# Revit family: 3034797 Sylvania Lighting Fixture GIOTTO335 LED G2 3000K SURFACE
name_source: partatom
category: Lighting Fixtures
revit_build: Autodesk Revit 2016 (Build: 20150220_1215(x64)
units: mm (PartAtom-declared; Revit-internal decimal feet)

## family parameters
Cut with Voids When Loaded = No
Host = Face
Light Source = Yes
OmniClass Number = 23.80.70.00
OmniClass Title = Lighting
Part Type = Normal
Room Calculation Point = No
Round Connector Dimension = Use Diameter
Shared = No

## types (1)
- 3034797 GIOTTO335 LED G2 SURFACE 3000K
    Apparent Load = 23 VA
    Assembly Code = D5020200
    AssetType = Fixed
    ClassificationName = Uniclass2015
    ClassificationValue = EF_70_80
    Color Filter = 16777215
    Cost = 0 $
    Default Elevation = 1219 mm
    Description = Ambient and decorative round, surface mounted LED bulkhead luminaire. White robust polycarbonate body with opal diffuser, 2111 lm, 23W, 92lm/W, 3000K, CRI 80, non-dimmable, 50,000 hours lumen maintenance. Drive current: 700mA, IP44, IK10, Class I, 220-240V, Energy class: A++, A+, A.
    Diameter_SYL = 335 mm  [stored 1.09908 ft]
    DiffuserRadius_SYL = 283 mm
    Dimming Lamp Color Temperature Shift = <None>
    DocumentationLiterature = http://www.sylvania-lighting.com
    DurationUnit = hours
    ElectricShockClassification = Class I
    Emit Shape Visible in Rendering = No
    Emit from Circle Diameter = 317 mm  [stored 1.04003 ft]
    ExpectedLife = 50000
    Height_SYL = 110 mm  [stored 0.360892 ft]
    IfcExportAs = IfcLightFixtureType
    IfcExportType = IfcLightFixtureType
    ImpactProtectionIndex = IK10
    IngressProtection = IP44
    Keynote = 16500
    Lamp = LED
    LampColourRenderingIndex = 80
    LampColourTemperature = 3000 K
    LampNominalLuminous = 2111 lm
    LampsType = LED
    LuminousEfficacy = 92 lm/W
    Manufacturer = Feilo Sylvania
    ManufacturerName = Feilo Sylvania
    Material = polycarbonate housing, polycarbonate diffuser
    Material_1_SYL = Polycarbonate_Sylvania_Giotto_White
    Material_2_SYL = Polycarbonate_Sylvania_Giotto_Opal
    Material_3_SYL = LED-Sylvania
    Material_4_SYL = <By Category>
    Model = GIOTTO335 LED G2 3000K SURFACE
    ModelNumber = 3034797
    ModelReference = GIOTTO335 LED G2 3000K SURFACE
    Name = GIOTTO335 LED G2 3000K SURFACE
    NominalDepth = 335 mm  [stored 1.09908 ft]
    NominalHeight = 110 mm  [stored 0.360892 ft]
    NominalLength = 335 mm  [stored 1.09908 ft]
    Photometric Web File = 3034797.ies
    PowerConsumption = 23 W
    PowerFactor = 0
    Tilt Angle = -90.00°
    Type Image = <None>
    TypeName = GIOTTO335 LED G2 3000K SURFACE
    URL = http://www.sylvania-lighting.com
    Voltage = 230 V
    Weight = 1.2 kg

note: [stored X ft] marks values corroborated as IEEE doubles in the binary element streams (Revit-internal decimal feet)

## geometry (parser evidence)
native form markers: Sweep x3
no freeform markers — native parametric forms only
